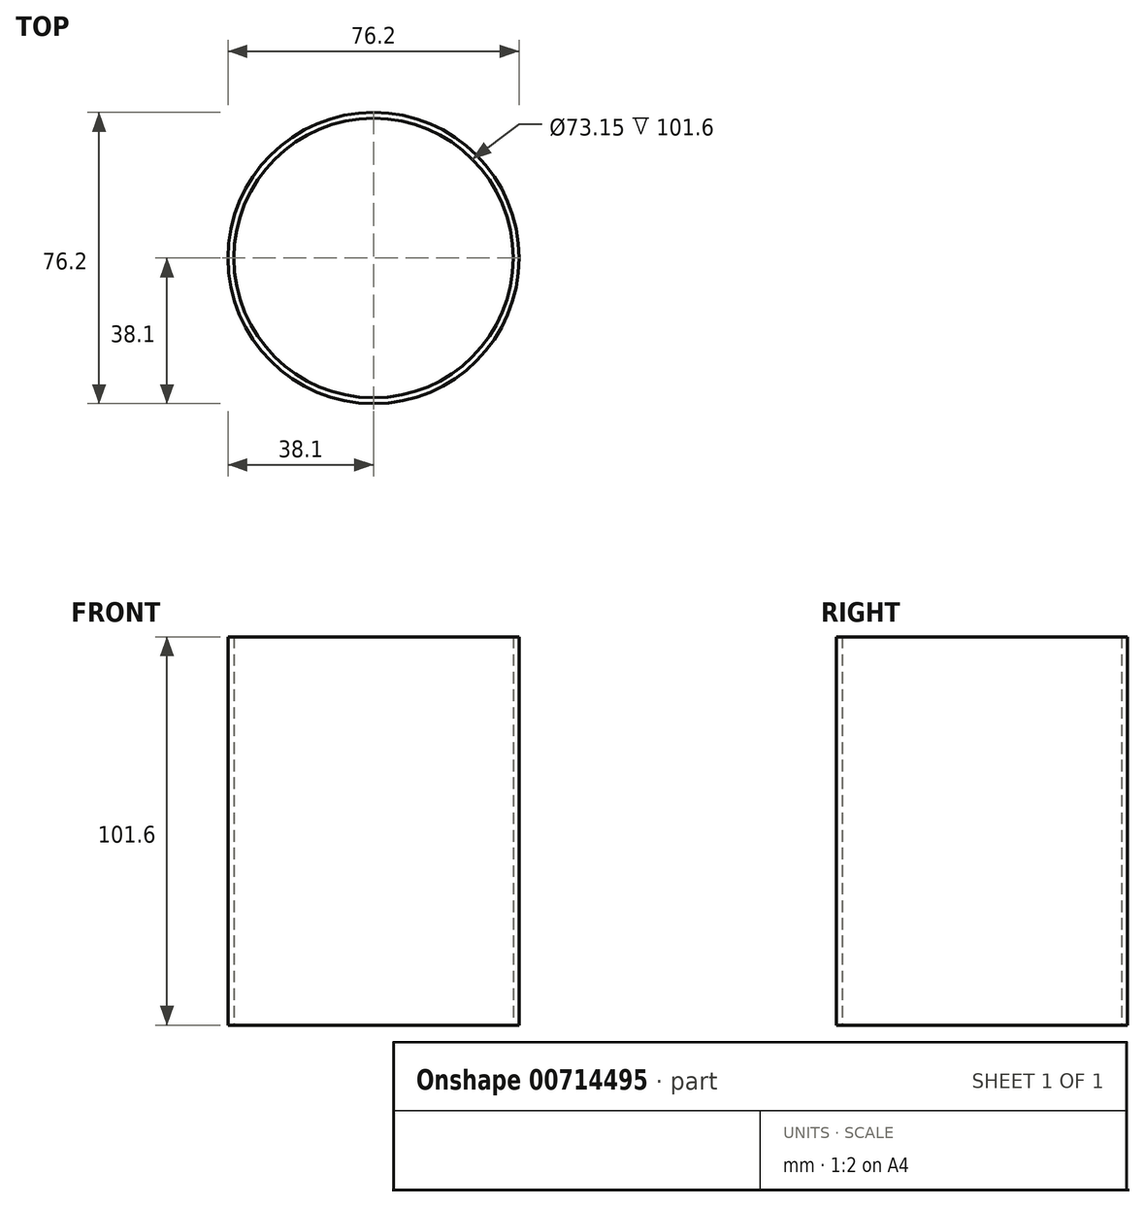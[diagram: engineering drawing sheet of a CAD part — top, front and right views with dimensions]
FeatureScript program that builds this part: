
annotation { "Feature Type Name" : "Feature", "Feature Type Description" : "" }
export const myFeature = defineFeature(function(context is Context, id is Id, definition is map)
    precondition{}
    {
        {
            var Q0;
            Q0=qCreatedBy(makeId("Top.planeOp"),FACE);
            var sketch = newSketch(context, id + "F0", { "sketchPlane" : qUnion([Q0])});
            skCircle(sketch, "E0", {"center": v(0, 0) * mm, "radius": 38.1 * mm});
            skCircle(sketch, "E1.0", {"center": v(0, 0) * mm, "radius": 36.58 * mm});
            skSolve(sketch);
        }
        {
            var Q0;
            Q0 = qSketchRegion(id + "F0", true);
            extrude(context, id + "F1", {"entities" : qUnion([Q0]), "depth" : 101.6 * mm, "offsetDistance" : 25.4 * mm});
        }
    });
